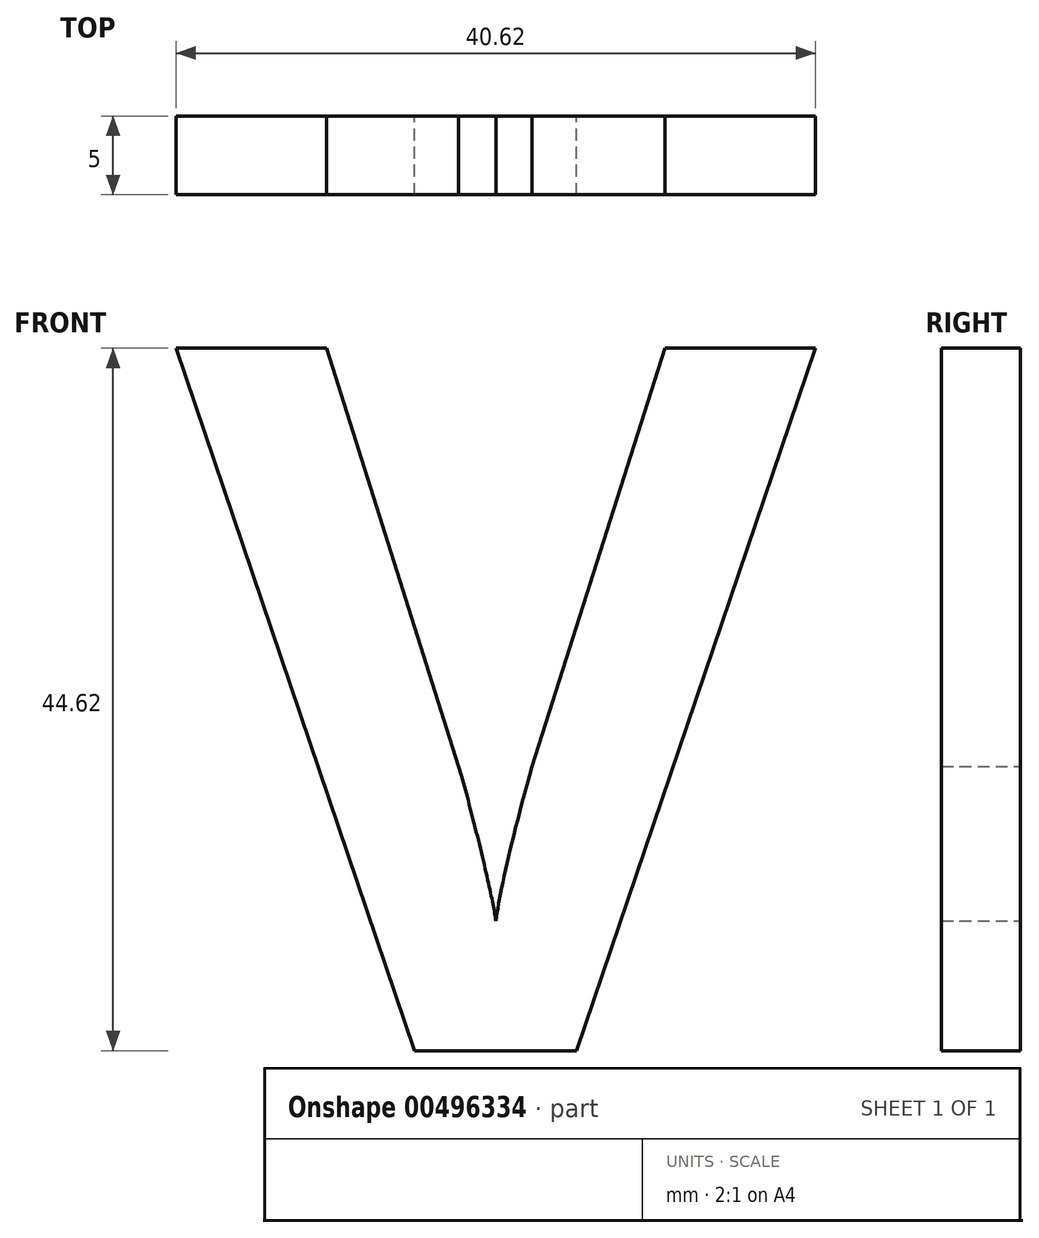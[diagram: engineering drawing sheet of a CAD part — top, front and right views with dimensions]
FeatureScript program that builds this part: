
annotation { "Feature Type Name" : "Feature", "Feature Type Description" : "" }
export const myFeature = defineFeature(function(context is Context, id is Id, definition is map)
    precondition{}
    {
        {
            var Q0;
            Q0=qCreatedBy(makeId("Front.planeOp"),FACE);
            var sketch = newSketch(context, id + "F0", { "sketchPlane" : qUnion([Q0])});
            skText(sketch, "E0", { "text": "V", "fontName": "OpenSans-Bold.ttf"});
            const initialGuessF0  = {"E0": [-0.0577, 0.01573, 1, 0, 0.045]};
            skSetInitialGuess(sketch, initialGuessF0);
            skSolve(sketch);
        }
        {
            var Q0;
            Q0=makeQuery(id+"F0.imprint","IMPRINT",FACE,{"disambiguationData":[TD([[makeQuery(id+"F0.imprint","IMPRINT",EDGE,{"derivedFrom":sQuery(id+"F0.wireOp",EDGE,"E0.sketch_text.stroke-0")}),-1.0]])]});
            extrude(context, id + "F1", {"entities" : qUnion([Q0]), "depth" : 5 * mm});
        }
    });
